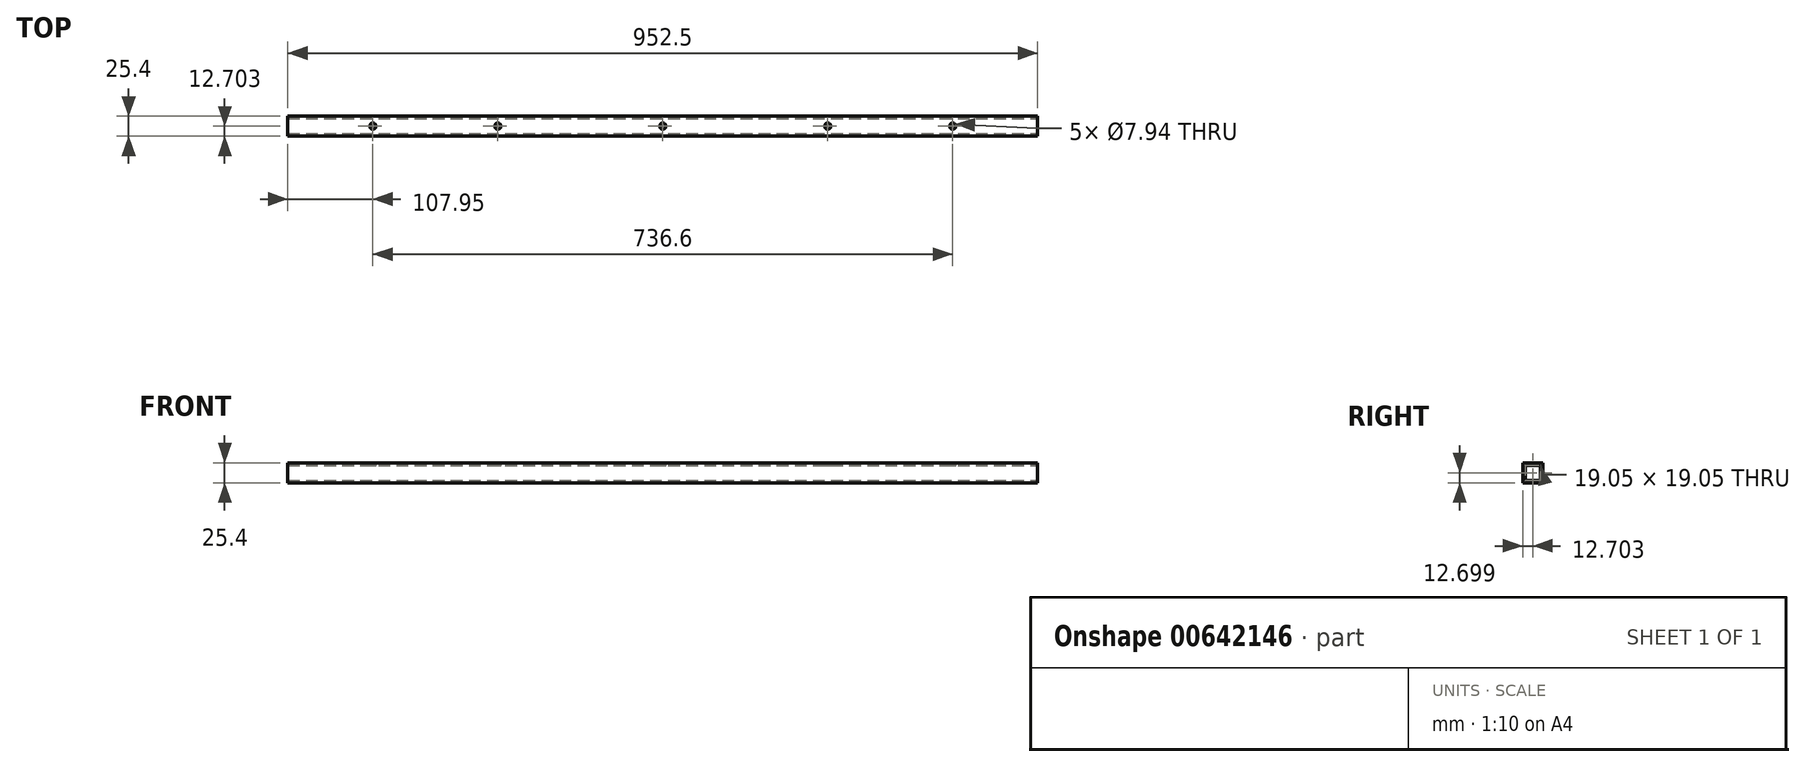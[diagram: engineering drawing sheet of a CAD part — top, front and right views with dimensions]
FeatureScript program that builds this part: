
annotation { "Feature Type Name" : "Feature", "Feature Type Description" : "" }
export const myFeature = defineFeature(function(context is Context, id is Id, definition is map)
    precondition{}
    {
        {
            var Q0;
            Q0=qCreatedBy(makeId("Right.planeOp"),FACE);
            var sketch = newSketch(context, id + "F0", { "sketchPlane" : qUnion([Q0])});
            skLineSegment(sketch, "E0", {"start": v(-60, 63.24) * mm, "end": v(-60, 37.84) * mm});
            skLineSegment(sketch, "E1", {"start": v(-60, 37.84) * mm, "end": v(-34.6, 37.84) * mm});
            skLineSegment(sketch, "E2", {"start": v(-34.6, 37.84) * mm, "end": v(-34.6, 63.24) * mm});
            skLineSegment(sketch, "E3", {"start": v(-34.6, 63.24) * mm, "end": v(-60, 63.24) * mm});
            skSolve(sketch);
        }
        {
            var Q0;
            Q0=makeQuery(id+"F0.imprint","IMPRINT",FACE,{"disambiguationData":[TD([[makeQuery(id+"F0.imprint","IMPRINT",EDGE,{"derivedFrom":sQuery(id+"F0.wireOp",EDGE,"E0")}),1.0]])]});
            extrude(context, id + "F1", {"entities" : qUnion([Q0]), "depth" : 952.5 * mm, "offsetDistance" : 25.4 * mm});
        }
        {
            var Q0;
            Q0=makeQuery(id+"F1.opExtrude","CAP_FACE",FACE,{"disambiguationData":[OSD([sQuery(id+"F0.wireOp",EDGE,"E0"),sQuery(id+"F0.wireOp",EDGE,"E1"),sQuery(id+"F0.wireOp",EDGE,"E2"),sQuery(id+"F0.wireOp",EDGE,"E3")])],"isStart":false});
            var sketch = newSketch(context, id + "F2", { "sketchPlane" : qUnion([Q0])});
            skPoint(sketch, "E4.oppositeSnap0", {"position": v(-40.96, 41.01) * mm});
            skPoint(sketch, "E5.orphan", {"position": v(-56.83, 63.24) * mm});
            skPoint(sketch, "E6.start.orphan", {"position": v(-56.83, 57.97) * mm});
            skPoint(sketch, "E7.end.orphan", {"position": v(-56.83, 60.06) * mm});
            skPoint(sketch, "E8", {"position": v(-37.78, 41.01) * mm});
            skPoint(sketch, "E9.end.orphan", {"position": v(-37.78, 37.84) * mm});
            skPoint(sketch, "E10.orphan", {"position": v(-34.6, 41.01) * mm});
            skPoint(sketch, "E11.start.orphan", {"position": v(-47.3, 37.84) * mm});
            skPoint(sketch, "E4.top.end.orphan", {"position": v(-47.3, 41.01) * mm});
            skLineSegment(sketch, "E12.bottom", {"start": v(-56.83, 60.06) * mm, "end": v(-37.78, 60.06) * mm});
            skLineSegment(sketch, "E12.top", {"start": v(-56.83, 41.01) * mm, "end": v(-37.78, 41.01) * mm});
            skLineSegment(sketch, "E12.left", {"start": v(-56.83, 60.06) * mm, "end": v(-56.83, 41.01) * mm});
            skLineSegment(sketch, "E12.right", {"start": v(-37.78, 60.06) * mm, "end": v(-37.78, 41.01) * mm});
            skSolve(sketch);
        }
        {
            var Q0;
            Q0=makeQuery(id+"F2.imprint","IMPRINT",FACE,{"disambiguationData":[TD([[makeQuery(id+"F2.imprint","IMPRINT",EDGE,{"derivedFrom":sQuery(id+"F2.wireOp",EDGE,"E12.bottom")}),-1.0]])]});
            extrude(context, id + "F3", {"entities" : qUnion([Q0]), "operationType" : NewBodyOperationType.REMOVE, "endBound" : BoundingType.THROUGH_ALL, "oppositeDirection" : true, "depth" : 25.4 * mm, "offsetDistance" : 25.4 * mm});
        }
        {
            var Q0;
            Q0=makeQuery(id+"F1.opExtrude","SWEPT_FACE",FACE,{"disambiguationData":[OSD([sQuery(id+"F0.wireOp",EDGE,"E3")])]});
            var sketch = newSketch(context, id + "F4", { "sketchPlane" : qUnion([Q0])});
            skPoint(sketch, "E13", {"position": v(476.25, -47.3) * mm});
            skPoint(sketch, "E14.end.orphan", {"position": v(0, -47.3) * mm});
            skPoint(sketch, "E15", {"position": v(266.7, -47.3) * mm});
            skPoint(sketch, "E16", {"position": v(107.95, -47.3) * mm});
            skPoint(sketch, "E17", {"position": v(685.8, -47.3) * mm});
            skPoint(sketch, "E18.start.orphan", {"position": v(952.5, -47.3) * mm});
            skPoint(sketch, "E19", {"position": v(844.55, -47.3) * mm});
            skSolve(sketch);
        }
        {
            var Q0;
            Q0=sQuery(id+"F4.wireOp",VERTEX,"E19");
            var Q1;
            Q1=sQuery(id+"F4.wireOp",VERTEX,"E17");
            var Q2;
            Q2=sQuery(id+"F4.wireOp",VERTEX,"E13");
            var Q3;
            Q3=sQuery(id+"F4.wireOp",VERTEX,"E15");
            var Q4;
            Q4=sQuery(id+"F4.wireOp",VERTEX,"E16");
            var Q5;
            Q5=makeQuery(id+"F1.opExtrude","SWEPT_BODY",BODY,{"disambiguationData":[OSD([sQuery(id+"F0.wireOp",EDGE,"E0"),sQuery(id+"F0.wireOp",EDGE,"E1"),sQuery(id+"F0.wireOp",EDGE,"E2"),sQuery(id+"F0.wireOp",EDGE,"E3")])]});
            hole(context, id + "F5", {"style" : HoleStyle.SIMPLE, "endStyle" : HoleEndStyle.BLIND, "standardTappedOrClearance" : lookupTablePath({ "standard" : "ANSI", "engagement" : "75%", "pitch" : "16 tpi", "size" : "3/8", "type" : "Tapped" }), "standardBlindInLast" : lookupTablePath({ "standard" : "ANSI", "engagement" : "75%", "pitch" : "16 tpi", "size" : "3/8", "type" : "Tapped" }), "holeDiameter" : 7.94 * mm, "majorDiameter" : 9.52 * mm, "showTappedDepth" : true, "holeDepth" : 17.48 * mm, "isTappedThrough" : true, "tappedDepth" : 12.71 * mm, "tapClearance" : 3, "locations" : qUnion([Q0, Q1, Q2, Q3, Q4]), "scope" : qUnion([Q5])});
        }
    });
